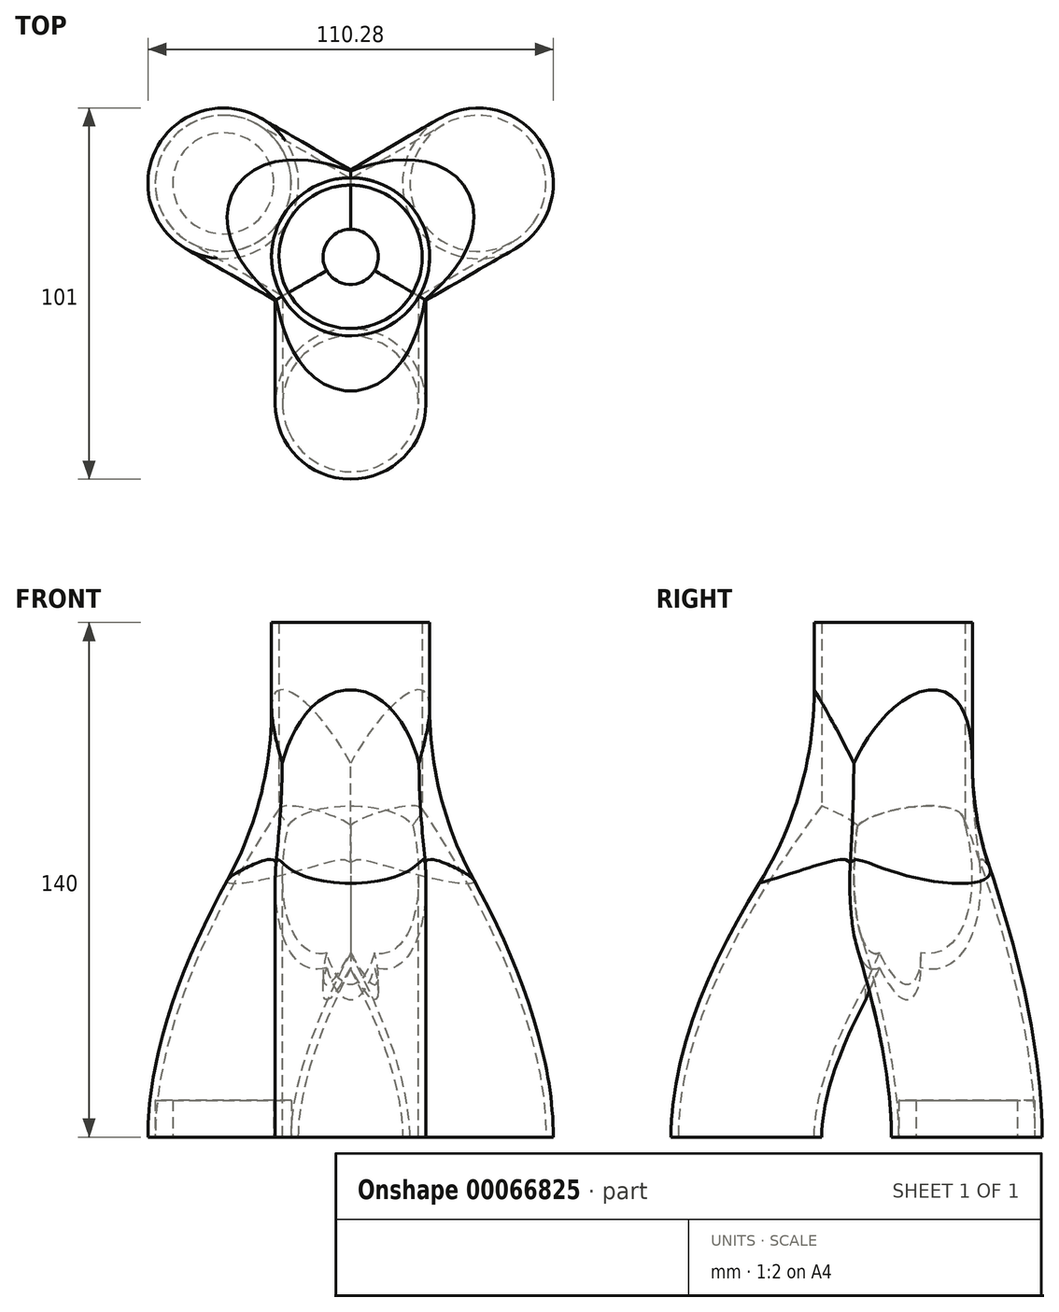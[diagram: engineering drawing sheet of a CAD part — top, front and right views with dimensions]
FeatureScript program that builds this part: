
annotation { "Feature Type Name" : "Feature", "Feature Type Description" : "" }
export const myFeature = defineFeature(function(context is Context, id is Id, definition is map)
    precondition{}
    {
        {
            var Q0;
            Q0=qCreatedBy(makeId("Top.planeOp"),FACE);
            var sketch = newSketch(context, id + "F0", { "sketchPlane" : qUnion([Q0])});
            skCircle(sketch, "E0", {"center": v(0, 0) * mm, "radius": 21.5 * mm});
            skSolve(sketch);
        }
        {
            var Q0;
            Q0=makeQuery(id+"F0.imprint","IMPRINT",FACE,{"disambiguationData":[TD([[makeQuery(id+"F0.imprint","IMPRINT",EDGE,{"derivedFrom":sQuery(id+"F0.wireOp",EDGE,"E0")}),1.0]])]});
            extrude(context, id + "F1", {"entities" : qUnion([Q0]), "depth" : 60 * mm});
        }
        {
            var Q0;
            Q0=qCreatedBy(makeId("Right.planeOp"),FACE);
            var sketch = newSketch(context, id + "F2", { "sketchPlane" : qUnion([Q0])});
            skFitSpline(sketch, "E1", {"points": [v(0, 5) * mm, v(-40, -80) * mm], "startDerivative": vector(-87.7, -109.44) * mm, "endDerivative": vector(0, -57.61) * mm});
            skLineSegment(sketch, "E2", {"start": v(-40, -80) * mm, "end": v(-40, -41.6) * mm, "construction": true});
            skSolve(sketch);
        }
        {
            var Q0;
            Q0=makeQuery(id+"F1.opExtrude","CAP_FACE",FACE,{"disambiguationData":[OSD([sQuery(id+"F0.wireOp",EDGE,"E0")])],"isStart":true});
            cPlane(context, id + "F3", {"entities" : qUnion([Q0]), "cplaneType" : CPlaneType.OFFSET, "offset" : 80 * mm, "width" : 150 * mm, "height" : 150 * mm});
        }
        {
            var Q0;
            Q0=qCreatedBy(id+"F3.planeOp",FACE);
            var sketch = newSketch(context, id + "F4", { "sketchPlane" : qUnion([Q0])});
            skCircle(sketch, "E3", {"center": v(0, 40) * mm, "radius": 20.5 * mm});
            skSolve(sketch);
        }
        {
            var Q0;
            Q0=makeQuery(id+"F4.imprint","IMPRINT",FACE,{"disambiguationData":[TD([[makeQuery(id+"F4.imprint","IMPRINT",EDGE,{"derivedFrom":sQuery(id+"F4.wireOp",EDGE,"E3")}),1.0]])]});
            var Q1;
            Q1=sQuery(id+"F2.wireOp",EDGE,"E1");
            sweep(context, id + "F5", {"operationType" : NewBodyOperationType.ADD, "profiles" : qUnion([Q0]), "path" : qUnion([Q1])});
        }
        {
            var Q0;
            Q0=makeQuery(id+"F1.opExtrude","SWEPT_BODY",BODY,{"disambiguationData":[OSD([sQuery(id+"F0.wireOp",EDGE,"E0")])]});
            var Q1;
            Q1=makeQuery(id+"F1.opExtrude","CAP_EDGE",EDGE,{"disambiguationData":[OSD([sQuery(id+"F0.wireOp",EDGE,"E0")])],"isStart":false});
            circularPattern(context, id + "F6", {"entities" : qUnion([Q0]), "axis" : qUnion([Q1]), "angle" : 360 * degree, "instanceCount" : 3, "equalSpace" : true});
        }
        {
            var Q0;
            Q0=makeQuery(id+"F1.opExtrude","SWEPT_BODY",BODY,{"disambiguationData":[OSD([sQuery(id+"F0.wireOp",EDGE,"E0")])]});
            var Q1;
            Q1=makeQuery(id+"F6.opPattern","COPY",BODY,{"derivedFrom":makeQuery(id+"F1.opExtrude","SWEPT_BODY",BODY,{"disambiguationData":[OSD([sQuery(id+"F0.wireOp",EDGE,"E0")])]}),"instanceName":"1"});
            var Q2;
            Q2=makeQuery(id+"F6.opPattern","COPY",BODY,{"derivedFrom":makeQuery(id+"F1.opExtrude","SWEPT_BODY",BODY,{"disambiguationData":[OSD([sQuery(id+"F0.wireOp",EDGE,"E0")])]}),"instanceName":"2"});
            booleanBodies(context, id + "F7", {"operationType" : BooleanOperationType.UNION, "tools" : qUnion([Q0, Q1, Q2])});
        }
        {
            var Q0;
            Q0=makeQuery(id+"F1.opExtrude","CAP_FACE",FACE,{"disambiguationData":[OSD([sQuery(id+"F0.wireOp",EDGE,"E0")])],"isStart":false});
            var Q1;
            Q1=makeQuery(id+"F5.opSweep","CAP_FACE",FACE,{"disambiguationData":[OSD([sQuery(id+"F2.wireOp",VERTEX,"E1.end"),sQuery(id+"F4.wireOp",EDGE,"E3")])],"isStart":true});
            var Q2;
            Q2=makeQuery(id+"F6.opPattern","COPY",FACE,{"derivedFrom":makeQuery(id+"F5.opSweep","CAP_FACE",FACE,{"disambiguationData":[OSD([sQuery(id+"F2.wireOp",VERTEX,"E1.end"),sQuery(id+"F4.wireOp",EDGE,"E3")])],"isStart":true}),"instanceName":"2"});
            var Q3;
            Q3=makeQuery(id+"F6.opPattern","COPY",FACE,{"derivedFrom":makeQuery(id+"F5.opSweep","CAP_FACE",FACE,{"disambiguationData":[OSD([sQuery(id+"F2.wireOp",VERTEX,"E1.end"),sQuery(id+"F4.wireOp",EDGE,"E3")])],"isStart":true}),"instanceName":"1"});
            var Q4;
            Q4=makeQuery(id+"F1.opExtrude","SWEPT_BODY",BODY,{"disambiguationData":[OSD([sQuery(id+"F0.wireOp",EDGE,"E0")])]});
            shell(context, id + "F8", {"entities" : qUnion([Q0, Q1, Q2, Q3]), "parts" : qUnion([Q4]), "thickness" : 2 * mm});
        }
        {
            var Q0;
            Q0=makeQuery(id+"F1.opExtrude","CAP_FACE",FACE,{"disambiguationData":[OSD([sQuery(id+"F0.wireOp",EDGE,"E0")])],"isStart":false});
            var sketch = newSketch(context, id + "F9", { "sketchPlane" : qUnion([Q0])});
            skCircle(sketch, "E4", {"center": v(0, 0) * mm, "radius": 7.5 * mm});
            skSolve(sketch);
        }
        {
            var Q0;
            Q0=makeQuery(id+"F9.imprint","IMPRINT",FACE,{"disambiguationData":[TD([[makeQuery(id+"F9.imprint","IMPRINT",EDGE,{"derivedFrom":sQuery(id+"F9.wireOp",EDGE,"E4")}),1.0]])]});
            extrude(context, id + "F10", {"entities" : qUnion([Q0]), "operationType" : NewBodyOperationType.REMOVE, "oppositeDirection" : true, "depth" : 145.02 * mm});
        }
        {
            var Q0;
            Q0=makeQuery(id+"F6.opPattern","COPY",FACE,{"derivedFrom":makeQuery(id+"F5.opSweep","CAP_FACE",FACE,{"disambiguationData":[OSD([sQuery(id+"F2.wireOp",VERTEX,"E1.end"),sQuery(id+"F4.wireOp",EDGE,"E3")])],"isStart":true}),"instanceName":"2"});
            var sketch = newSketch(context, id + "F11", { "sketchPlane" : qUnion([Q0])});
            skCircle(sketch, "E5", {"center": v(-34.64, -20) * mm, "radius": 13.75 * mm});
            skCircle(sketch, "E6", {"center": v(-34.64, -20) * mm, "radius": 18.5 * mm});
            skSolve(sketch);
        }
        {
            var Q0;
            Q0=makeQuery(id+"F5.boolean.opBoolean","INTERSECT",EDGE,{"derivedFrom":[makeQuery(id+"F1.opExtrude","SWEPT_FACE",FACE,{"disambiguationData":[OSD([sQuery(id+"F0.wireOp",EDGE,"E0")])]}),makeQuery(id+"F5.opSweep","SWEPT_FACE",FACE,{"disambiguationData":[OSD([sQuery(id+"F2.wireOp",EDGE,"E1"),sQuery(id+"F4.wireOp",EDGE,"E3")])]})]});
            var Q1;
            {var subQ0=makeQuery(id+"F1.opExtrude","SWEPT_FACE",FACE,{"disambiguationData":[OSD([sQuery(id+"F0.wireOp",EDGE,"E0")])]});Q1=makeQuery(id+"F7.opBoolean","INTERSECT",EDGE,{"derivedFrom":[subQ0,makeQuery(id+"F6.opPattern","COPY",FACE,{"derivedFrom":subQ0,"instanceName":"2"})]});}
            var Q2;
            {var subQ0=makeQuery(id+"F1.opExtrude","SWEPT_FACE",FACE,{"disambiguationData":[OSD([sQuery(id+"F0.wireOp",EDGE,"E0")])]});Q2=makeQuery(id+"F7.opBoolean","INTERSECT",EDGE,{"derivedFrom":[subQ0,makeQuery(id+"F6.opPattern","COPY",FACE,{"derivedFrom":subQ0,"instanceName":"1"})]});}
            fillet(context, id + "F12", {"entities" : qUnion([Q0, Q1, Q2]), "radius" : 100 * mm, "tangentPropagation" : true, "allowEdgeOverflow" : false});
        }
        {
            var Q0;
            Q0=makeQuery(id+"F11.imprint","IMPRINT",FACE,{"disambiguationData":[TD([[makeQuery(id+"F11.imprint","IMPRINT",EDGE,{"derivedFrom":sQuery(id+"F11.wireOp",EDGE,"E5")}),-1.0]])]});
            extrude(context, id + "F13", {"entities" : qUnion([Q0]), "oppositeDirection" : true, "depth" : 10 * mm});
        }
    });
